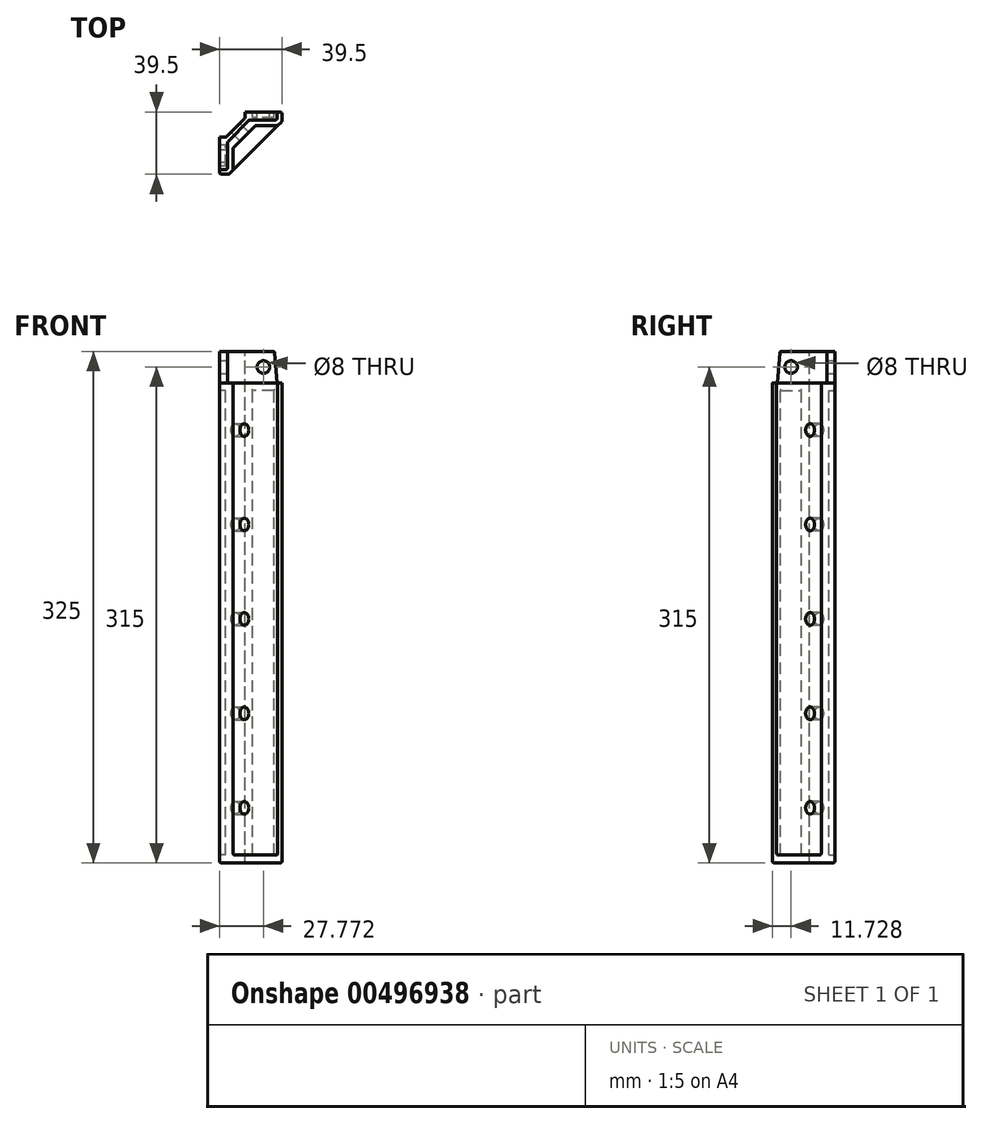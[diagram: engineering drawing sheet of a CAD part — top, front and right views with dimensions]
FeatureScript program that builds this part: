
annotation { "Feature Type Name" : "Feature", "Feature Type Description" : "" }
export const myFeature = defineFeature(function(context is Context, id is Id, definition is map)
    precondition{}
    {
        {
            var Q0;
            Q0=qCreatedBy(makeId("Top.planeOp"),FACE);
            var sketch = newSketch(context, id + "F0", { "sketchPlane" : qUnion([Q0])});
            skLineSegment(sketch, "E0", {"start": v(0, 30.13) * mm, "end": v(0, -27.95) * mm, "construction": true});
            skLineSegment(sketch, "E1", {"start": v(-25.65, 0) * mm, "end": v(27.57, 0) * mm, "construction": true});
            skLineSegment(sketch, "E2.bottom", {"start": v(-19.75, 19.75) * mm, "end": v(19.75, 19.75) * mm});
            skLineSegment(sketch, "E2.top", {"start": v(-19.75, -19.75) * mm, "end": v(-13.75, -19.75) * mm});
            skLineSegment(sketch, "E2.left", {"start": v(-19.75, 19.75) * mm, "end": v(-19.75, -19.75) * mm});
            skLineSegment(sketch, "E2.right", {"start": v(19.75, 19.75) * mm, "end": v(19.75, 13.75) * mm});
            skLineSegment(sketch, "E3", {"start": v(-13.75, -19.75) * mm, "end": v(19.75, 13.75) * mm});
            skSolve(sketch);
        }
        {
            var Q0;
            Q0=qSketchRegion(id+"F0",true);
            extrude(context, id + "F1", {"entities" : qUnion([Q0]), "oppositeDirection" : true, "depth" : 305 * mm, "symmetric" : true});
        }
        {
            var Q0;
            Q0=makeQuery(id+"F1.opExtrude","CAP_FACE",FACE,{"disambiguationData":[OSD([sQuery(id+"F0.wireOp",EDGE,"E2.bottom"),sQuery(id+"F0.wireOp",EDGE,"E2.top"),sQuery(id+"F0.wireOp",EDGE,"E2.left"),sQuery(id+"F0.wireOp",EDGE,"E2.right"),sQuery(id+"F0.wireOp",EDGE,"E3")])],"isStart":true});
            var sketch = newSketch(context, id + "F2", { "sketchPlane" : qUnion([Q0])});
            skLineSegment(sketch, "E4", {"start": v(3, -3) * mm, "end": v(-19.75, 19.75) * mm, "construction": true});
            skLineSegment(sketch, "E5", {"start": v(3, -3) * mm, "end": v(17.14, 11.14) * mm});
            skLineSegment(sketch, "E6", {"start": v(3, -3) * mm, "end": v(-11.14, -17.14) * mm});
            skLineSegment(sketch, "E7", {"start": v(-11.14, -3) * mm, "end": v(3, 11.14) * mm});
            skLineSegment(sketch, "E8", {"start": v(-11.14, -17.14) * mm, "end": v(-11.14, -3) * mm});
            skLineSegment(sketch, "E9", {"start": v(3, 11.14) * mm, "end": v(17.14, 11.14) * mm});
            skSolve(sketch);
        }
        {
            var Q0;
            Q0=qSketchRegion(id+"F2",true);
            extrude(context, id + "F3", {"entities" : qUnion([Q0]), "operationType" : NewBodyOperationType.REMOVE, "oppositeDirection" : true, "depth" : 300 * mm});
        }
        {
            var Q0;
            Q0=makeQuery(id+"F1.opExtrude","CAP_FACE",FACE,{"disambiguationData":[OSD([sQuery(id+"F0.wireOp",EDGE,"E2.bottom"),sQuery(id+"F0.wireOp",EDGE,"E2.top"),sQuery(id+"F0.wireOp",EDGE,"E2.left"),sQuery(id+"F0.wireOp",EDGE,"E2.right"),sQuery(id+"F0.wireOp",EDGE,"E3")])],"isStart":true});
            var sketch = newSketch(context, id + "F4", { "sketchPlane" : qUnion([Q0])});
            skPoint(sketch, "E10.orphan", {"position": v(-19.75, -19.75) * mm});
            skPoint(sketch, "E11.orphan", {"position": v(19.75, 19.75) * mm});
            skLineSegment(sketch, "E12", {"start": v(-19.75, 19.75) * mm, "end": v(-4.07, 4.07) * mm, "construction": true});
            skLineSegment(sketch, "E13", {"start": v(-15.75, 3.7) * mm, "end": v(-19.75, 3.7) * mm});
            skLineSegment(sketch, "E14", {"start": v(-3.7, 15.75) * mm, "end": v(-3.7, 19.75) * mm});
            skLineSegment(sketch, "E15", {"start": v(-3.7, 19.75) * mm, "end": v(-19.75, 19.75) * mm});
            skLineSegment(sketch, "E16", {"start": v(-19.75, 19.75) * mm, "end": v(-19.75, 3.7) * mm});
            skLineSegment(sketch, "E17", {"start": v(-3.7, 15.75) * mm, "end": v(-15.75, 3.7) * mm});
            skPoint(sketch, "E18.orphan", {"position": v(-14.68, 3.7) * mm});
            skPoint(sketch, "E19.orphan", {"position": v(-3.7, 13.6) * mm});
            skSolve(sketch);
        }
        {
            var Q0;
            Q0=qSketchRegion(id+"F4",true);
            extrude(context, id + "F5", {"entities" : qUnion([Q0]), "operationType" : NewBodyOperationType.REMOVE, "endBound" : BoundingType.THROUGH_ALL, "oppositeDirection" : true, "depth" : 25 * mm});
        }
        {
            var Q0;
            Q0=makeQuery(id+"F1.opExtrude","CAP_FACE",FACE,{"disambiguationData":[OSD([sQuery(id+"F0.wireOp",EDGE,"E2.bottom"),sQuery(id+"F0.wireOp",EDGE,"E2.top"),sQuery(id+"F0.wireOp",EDGE,"E2.left"),sQuery(id+"F0.wireOp",EDGE,"E2.right"),sQuery(id+"F0.wireOp",EDGE,"E3")])],"isStart":true});
            var sketch = newSketch(context, id + "F6", { "sketchPlane" : qUnion([Q0])});
            skLineSegment(sketch, "E20.0", {"start": v(1.3, 16.14) * mm, "end": v(14.75, 16.14) * mm});
            skLineSegment(sketch, "E20.1", {"start": v(14.75, 19.75) * mm, "end": v(14.75, 16.14) * mm});
            skLineSegment(sketch, "E21.0", {"start": v(1.3, 16.14) * mm, "end": v(1.3, 19.75) * mm});
            skLineSegment(sketch, "E22", {"start": v(14.75, 19.75) * mm, "end": v(1.3, 19.75) * mm});
            skLineSegment(sketch, "E23.0", {"start": v(-16.14, -14.75) * mm, "end": v(-16.14, -1.3) * mm});
            skLineSegment(sketch, "E23.1", {"start": v(-19.75, -14.75) * mm, "end": v(-16.14, -14.75) * mm});
            skLineSegment(sketch, "E24.0", {"start": v(-16.14, -1.3) * mm, "end": v(-19.75, -1.3) * mm});
            skPoint(sketch, "E25.orphan", {"position": v(-12.53, -1.3) * mm});
            skLineSegment(sketch, "E26", {"start": v(-19.75, -14.75) * mm, "end": v(-19.75, -1.3) * mm});
            skSolve(sketch);
        }
        {
            var Q0;
            Q0=qSketchRegion(id+"F6",true);
            extrude(context, id + "F7", {"entities" : qUnion([Q0]), "operationType" : NewBodyOperationType.REMOVE, "endBound" : BoundingType.THROUGH_ALL, "oppositeDirection" : true, "depth" : 25 * mm});
        }
        {
            var Q0;
            {var subQ1=sQuery(id+"F0.wireOp",EDGE,"E2.right");var subQ4=sQuery(id+"F0.wireOp",EDGE,"E2.bottom");Q0=makeQuery(id+"F7.boolean.opBoolean","SPLIT",FACE,{"disambiguationData":[TD([makeQuery(id+"F1.opExtrude","SWEPT_FACE",FACE,{"disambiguationData":[OSD([subQ1])]})])],"derivedFrom":makeQuery(id+"F1.opExtrude","SWEPT_FACE",FACE,{"disambiguationData":[OSD([subQ4])]})});}
            var sketch = newSketch(context, id + "F8", { "sketchPlane" : qUnion([Q0])});
            skLineSegment(sketch, "E27.bottom", {"start": v(-14.75, 152.5) * mm, "end": v(-1.3, 152.5) * mm});
            skLineSegment(sketch, "E27.top", {"start": v(-14.75, 147.5) * mm, "end": v(-1.3, 147.5) * mm});
            skLineSegment(sketch, "E27.left", {"start": v(-14.75, 152.5) * mm, "end": v(-14.75, 147.5) * mm});
            skLineSegment(sketch, "E27.right", {"start": v(-1.3, 152.5) * mm, "end": v(-1.3, 147.5) * mm});
            skLineSegment(sketch, "E28.bottom", {"start": v(-14.75, -152.5) * mm, "end": v(-1.3, -152.5) * mm});
            skLineSegment(sketch, "E28.top", {"start": v(-14.75, -147.5) * mm, "end": v(-1.3, -147.5) * mm});
            skLineSegment(sketch, "E28.left", {"start": v(-14.75, -152.5) * mm, "end": v(-14.75, -147.5) * mm});
            skLineSegment(sketch, "E28.right", {"start": v(-1.3, -152.5) * mm, "end": v(-1.3, -147.5) * mm});
            skSolve(sketch);
        }
        {
            var Q0;
            Q0=qSketchRegion(id+"F8",true);
            var Q1;
            Q1=makeQuery(id+"F7.boolean.opBoolean","COPY",FACE,{"derivedFrom":makeQuery(id+"F7.opExtrude","SWEPT_FACE",FACE,{"disambiguationData":[OSD([sQuery(id+"F6.wireOp",EDGE,"E20.0")])]})});
            extrude(context, id + "F9", {"entities" : qUnion([Q0]), "operationType" : NewBodyOperationType.ADD, "endBound" : BoundingType.UP_TO_SURFACE, "oppositeDirection" : true, "endBoundEntityFace" : qUnion([Q1]), "depth" : 25 * mm});
        }
        {
            var Q0;
            {var subQ2=sQuery(id+"F0.wireOp",EDGE,"E2.left");var subQ3=sQuery(id+"F0.wireOp",EDGE,"E2.top");Q0=makeQuery(id+"F7.boolean.opBoolean","SPLIT",FACE,{"disambiguationData":[TD([makeQuery(id+"F1.opExtrude","SWEPT_FACE",FACE,{"disambiguationData":[OSD([subQ3])]})])],"derivedFrom":makeQuery(id+"F1.opExtrude","SWEPT_FACE",FACE,{"disambiguationData":[OSD([subQ2])]})});}
            var sketch = newSketch(context, id + "F10", { "sketchPlane" : qUnion([Q0])});
            skLineSegment(sketch, "E29.bottom", {"start": v(14.75, 152.5) * mm, "end": v(1.3, 152.5) * mm});
            skLineSegment(sketch, "E29.top", {"start": v(14.75, 147.5) * mm, "end": v(1.3, 147.5) * mm});
            skLineSegment(sketch, "E29.left", {"start": v(14.75, 152.5) * mm, "end": v(14.75, 147.5) * mm});
            skLineSegment(sketch, "E29.right", {"start": v(1.3, 152.5) * mm, "end": v(1.3, 147.5) * mm});
            skLineSegment(sketch, "E30.bottom", {"start": v(14.75, -152.5) * mm, "end": v(1.3, -152.5) * mm});
            skLineSegment(sketch, "E30.top", {"start": v(14.75, -147.5) * mm, "end": v(1.3, -147.5) * mm});
            skLineSegment(sketch, "E30.left", {"start": v(14.75, -152.5) * mm, "end": v(14.75, -147.5) * mm});
            skLineSegment(sketch, "E30.right", {"start": v(1.3, -152.5) * mm, "end": v(1.3, -147.5) * mm});
            skSolve(sketch);
        }
        {
            var Q0;
            Q0=qSketchRegion(id+"F10",true);
            var Q1;
            Q1=makeQuery(id+"F7.boolean.opBoolean","COPY",FACE,{"derivedFrom":makeQuery(id+"F7.opExtrude","SWEPT_FACE",FACE,{"disambiguationData":[OSD([sQuery(id+"F6.wireOp",EDGE,"E23.0")])]})});
            extrude(context, id + "F11", {"entities" : qUnion([Q0]), "operationType" : NewBodyOperationType.ADD, "endBound" : BoundingType.UP_TO_SURFACE, "oppositeDirection" : true, "endBoundEntityFace" : qUnion([Q1]), "depth" : 25 * mm});
        }
        {
            var Q0;
            {var subQ2=sQuery(id+"F0.wireOp",EDGE,"E2.left");var subQ3=sQuery(id+"F0.wireOp",EDGE,"E2.top");var subQ7=makeQuery(id+"F1.opExtrude","SWEPT_FACE",FACE,{"disambiguationData":[OSD([subQ2])]});Q0=makeQuery(id+"F11.boolean.opBoolean","MERGE",FACE,{"derivedFrom":[makeQuery(id+"F7.boolean.opBoolean","SPLIT",FACE,{"disambiguationData":[TD([makeQuery(id+"F1.opExtrude","SWEPT_FACE",FACE,{"disambiguationData":[OSD([subQ3])]})])],"derivedFrom":subQ7}),makeQuery(id+"F7.boolean.opBoolean","SPLIT",FACE,{"disambiguationData":[TD([makeQuery(id+"F5.boolean.opBoolean","COPY",FACE,{"derivedFrom":makeQuery(id+"F5.opExtrude","SWEPT_FACE",FACE,{"disambiguationData":[OSD([sQuery(id+"F4.wireOp",EDGE,"E13")])]})})])],"derivedFrom":subQ7}),makeQuery(id+"F11.opExtrude","CAP_FACE",FACE,{"disambiguationData":[OSD([sQuery(id+"F10.wireOp",EDGE,"E29.bottom"),sQuery(id+"F10.wireOp",EDGE,"E29.top"),sQuery(id+"F10.wireOp",EDGE,"E29.left"),sQuery(id+"F10.wireOp",EDGE,"E29.right")])],"isStart":true}),makeQuery(id+"F11.opExtrude","CAP_FACE",FACE,{"disambiguationData":[OSD([sQuery(id+"F10.wireOp",EDGE,"E30.bottom"),sQuery(id+"F10.wireOp",EDGE,"E30.top"),sQuery(id+"F10.wireOp",EDGE,"E30.left"),sQuery(id+"F10.wireOp",EDGE,"E30.right")])],"isStart":true})]});}
            var sketch = newSketch(context, id + "F12", { "sketchPlane" : qUnion([Q0])});
            skLineSegment(sketch, "E31", {"start": v(8.02, 152.5) * mm, "end": v(8.02, 172.5) * mm, "construction": true});
            skLineSegment(sketch, "E32", {"start": v(0, 0) * mm, "end": v(35.4, 0) * mm, "construction": true});
            skPoint(sketch, "E32.endSnap0", {"position": v(19.75, 0) * mm});
            skLineSegment(sketch, "E33.MirrorCS", {"start": v(16.04, 0) * mm, "end": v(-19.35, 0) * mm, "construction": true});
            skLineSegment(sketch, "E34", {"start": v(16.75, 152.5) * mm, "end": v(-0.7, 152.5) * mm});
            skLineSegment(sketch, "E35", {"start": v(16.75, 152.5) * mm, "end": v(15.02, 172.5) * mm});
            skLineSegment(sketch, "E36", {"start": v(15.02, 172.5) * mm, "end": v(8.02, 172.5) * mm});
            skLineSegment(sketch, "E37", {"start": v(8.02, 172.5) * mm, "end": v(1.02, 172.5) * mm});
            skLineSegment(sketch, "E38", {"start": v(1.02, 172.5) * mm, "end": v(-0.7, 152.5) * mm});
            skLineSegment(sketch, "E39.MirrorCS", {"start": v(-0.7, 152.5) * mm, "end": v(1.02, 172.5) * mm});
            skSolve(sketch);
        }
        {
            var Q0;
            Q0=qSketchRegion(id+"F12",true);
            extrude(context, id + "F13", {"entities" : qUnion([Q0]), "operationType" : NewBodyOperationType.ADD, "oppositeDirection" : true, "depth" : 5 * mm});
        }
        {
            var Q0;
            {var subQ1=sQuery(id+"F0.wireOp",EDGE,"E2.right");var subQ4=sQuery(id+"F0.wireOp",EDGE,"E2.bottom");var subQ7=makeQuery(id+"F1.opExtrude","SWEPT_FACE",FACE,{"disambiguationData":[OSD([subQ4])]});Q0=makeQuery(id+"F9.boolean.opBoolean","MERGE",FACE,{"derivedFrom":[makeQuery(id+"F7.boolean.opBoolean","SPLIT",FACE,{"disambiguationData":[TD([makeQuery(id+"F1.opExtrude","SWEPT_FACE",FACE,{"disambiguationData":[OSD([subQ1])]})])],"derivedFrom":subQ7}),makeQuery(id+"F7.boolean.opBoolean","SPLIT",FACE,{"disambiguationData":[TD([makeQuery(id+"F5.boolean.opBoolean","COPY",FACE,{"derivedFrom":makeQuery(id+"F5.opExtrude","SWEPT_FACE",FACE,{"disambiguationData":[OSD([sQuery(id+"F4.wireOp",EDGE,"E14")])]})})])],"derivedFrom":subQ7}),makeQuery(id+"F9.opExtrude","CAP_FACE",FACE,{"disambiguationData":[OSD([sQuery(id+"F8.wireOp",EDGE,"E27.bottom"),sQuery(id+"F8.wireOp",EDGE,"E27.top"),sQuery(id+"F8.wireOp",EDGE,"E27.left"),sQuery(id+"F8.wireOp",EDGE,"E27.right")])],"isStart":true}),makeQuery(id+"F9.opExtrude","CAP_FACE",FACE,{"disambiguationData":[OSD([sQuery(id+"F8.wireOp",EDGE,"E28.bottom"),sQuery(id+"F8.wireOp",EDGE,"E28.top"),sQuery(id+"F8.wireOp",EDGE,"E28.left"),sQuery(id+"F8.wireOp",EDGE,"E28.right")])],"isStart":true})]});}
            var sketch = newSketch(context, id + "F14", { "sketchPlane" : qUnion([Q0])});
            skLineSegment(sketch, "E40", {"start": v(-8.02, 152.5) * mm, "end": v(-8.02, 172.66) * mm, "construction": true});
            skPoint(sketch, "E40.endSnap0", {"position": v(-8.02, 152.5) * mm});
            skLineSegment(sketch, "E41", {"start": v(-15.02, 172.5) * mm, "end": v(-1.02, 172.5) * mm});
            skLineSegment(sketch, "E42", {"start": v(0, 0) * mm, "end": v(-60.6, 0) * mm, "construction": true});
            skPoint(sketch, "E42.endSnap0", {"position": v(-14.75, 0) * mm});
            skLineSegment(sketch, "E43", {"start": v(-15.02, 172.5) * mm, "end": v(-16.75, 152.5) * mm});
            skLineSegment(sketch, "E44", {"start": v(-1.02, 172.5) * mm, "end": v(0.7, 152.5) * mm});
            skLineSegment(sketch, "E45", {"start": v(0.7, 152.5) * mm, "end": v(-16.75, 152.5) * mm});
            skSolve(sketch);
        }
        {
            var Q0;
            Q0=qSketchRegion(id+"F14",true);
            extrude(context, id + "F15", {"entities" : qUnion([Q0]), "operationType" : NewBodyOperationType.ADD, "oppositeDirection" : true, "depth" : 5 * mm});
        }
        {
            var Q0;
            {var subQ1=sQuery(id+"F0.wireOp",EDGE,"E2.right");var subQ4=sQuery(id+"F0.wireOp",EDGE,"E2.bottom");var subQ7=makeQuery(id+"F1.opExtrude","SWEPT_FACE",FACE,{"disambiguationData":[OSD([subQ4])]});Q0=makeQuery(id+"F15.boolean.opBoolean","MERGE",FACE,{"derivedFrom":[makeQuery(id+"F9.boolean.opBoolean","MERGE",FACE,{"derivedFrom":[makeQuery(id+"F7.boolean.opBoolean","SPLIT",FACE,{"disambiguationData":[TD([makeQuery(id+"F1.opExtrude","SWEPT_FACE",FACE,{"disambiguationData":[OSD([subQ1])]})])],"derivedFrom":subQ7}),makeQuery(id+"F7.boolean.opBoolean","SPLIT",FACE,{"disambiguationData":[TD([makeQuery(id+"F5.boolean.opBoolean","COPY",FACE,{"derivedFrom":makeQuery(id+"F5.opExtrude","SWEPT_FACE",FACE,{"disambiguationData":[OSD([sQuery(id+"F4.wireOp",EDGE,"E14")])]})})])],"derivedFrom":subQ7}),makeQuery(id+"F9.opExtrude","CAP_FACE",FACE,{"disambiguationData":[OSD([sQuery(id+"F8.wireOp",EDGE,"E27.bottom"),sQuery(id+"F8.wireOp",EDGE,"E27.top"),sQuery(id+"F8.wireOp",EDGE,"E27.left"),sQuery(id+"F8.wireOp",EDGE,"E27.right")])],"isStart":true}),makeQuery(id+"F9.opExtrude","CAP_FACE",FACE,{"disambiguationData":[OSD([sQuery(id+"F8.wireOp",EDGE,"E28.bottom"),sQuery(id+"F8.wireOp",EDGE,"E28.top"),sQuery(id+"F8.wireOp",EDGE,"E28.left"),sQuery(id+"F8.wireOp",EDGE,"E28.right")])],"isStart":true})]}),makeQuery(id+"F15.opExtrude","CAP_FACE",FACE,{"disambiguationData":[OSD([sQuery(id+"F14.wireOp",EDGE,"AjdLOBUI-PND2-HRux-vW9i-I60BuJFxOAxo"),sQuery(id+"F14.wireOp",EDGE,"m2E0O1S7-ugW4-w8lP-xUBK-8UGrL3XVD3p1"),sQuery(id+"F14.wireOp",EDGE,"E41"),sQuery(id+"F14.wireOp",EDGE,"z751VbyZ-Eswl-sp4i-D6d8-2ebrKqnJ25gN")])],"isStart":true}),makeQuery(id+"F15.opExtrude","CAP_FACE",FACE,{"disambiguationData":[OSD([sQuery(id+"F14.wireOp",EDGE,"9fced805-f766-4b14-a849-f1590210c0c81.MirrorCS"),sQuery(id+"F14.wireOp",EDGE,"9fced805-f766-4b14-a849-f1590210c0c82.MirrorCS"),sQuery(id+"F14.wireOp",EDGE,"9fced805-f766-4b14-a849-f1590210c0c83.MirrorCS"),sQuery(id+"F14.wireOp",EDGE,"9fced805-f766-4b14-a849-f1590210c0c84.MirrorCS")])],"isStart":true})]});}
            var sketch = newSketch(context, id + "F16", { "sketchPlane" : qUnion([Q0])});
            skLineSegment(sketch, "E46", {"start": v(-8.02, 172.5) * mm, "end": v(-8.02, -66.14) * mm, "construction": true});
            skCircle(sketch, "E47", {"center": v(-8.02, 162.5) * mm, "radius": 4 * mm});
            skSolve(sketch);
        }
        {
            var Q0;
            Q0=qSketchRegion(id+"F16",true);
            extrude(context, id + "F17", {"entities" : qUnion([Q0]), "operationType" : NewBodyOperationType.REMOVE, "endBound" : BoundingType.THROUGH_ALL, "oppositeDirection" : true, "depth" : 25 * mm});
        }
        {
            var Q0;
            Q0=makeQuery(id+"F3.boolean.opBoolean","COPY",FACE,{"derivedFrom":makeQuery(id+"F3.opExtrude","SWEPT_FACE",FACE,{"disambiguationData":[OSD([sQuery(id+"F2.wireOp",EDGE,"E7")])]})});
            var sketch = newSketch(context, id + "F18", { "sketchPlane" : qUnion([Q0])});
            skLineSegment(sketch, "E48", {"start": v(0, 152.5) * mm, "end": v(0, -147.5) * mm, "construction": true});
            skLineSegment(sketch, "E49", {"start": v(0, 2.5) * mm, "end": v(10, 2.5) * mm, "construction": true});
            skCircle(sketch, "E50", {"center": v(0, 122.5) * mm, "radius": 4 * mm});
            skCircle(sketch, "E51", {"center": v(0, 62.5) * mm, "radius": 4 * mm});
            skCircle(sketch, "E52.MirrorC", {"center": v(0, -117.5) * mm, "radius": 4 * mm});
            skCircle(sketch, "E53.MirrorC", {"center": v(0, -57.5) * mm, "radius": 4 * mm});
            skCircle(sketch, "E54", {"center": v(0, 2.5) * mm, "radius": 4 * mm});
            skSolve(sketch);
        }
        {
            var Q0;
            Q0=qSketchRegion(id+"F18",true);
            extrude(context, id + "F19", {"entities" : qUnion([Q0]), "operationType" : NewBodyOperationType.REMOVE, "endBound" : BoundingType.THROUGH_ALL, "oppositeDirection" : true, "depth" : 25 * mm});
        }
        {
            var Q0;
            Q0=makeQuery(id+"F13.opExtrude","CAP_FACE",FACE,{"disambiguationData":[OSD([sQuery(id+"F12.wireOp",EDGE,"E34"),sQuery(id+"F12.wireOp",EDGE,"E35"),sQuery(id+"F12.wireOp",EDGE,"E36"),sQuery(id+"F12.wireOp",EDGE,"E37"),sQuery(id+"F12.wireOp",EDGE,"E39.MirrorCS")])],"isStart":false});
            var sketch = newSketch(context, id + "F20", { "sketchPlane" : qUnion([Q0])});
            skLineSegment(sketch, "E55", {"start": v(-8.02, 172.5) * mm, "end": v(-8.02, -22.5) * mm, "construction": true});
            skPoint(sketch, "E55.endSnap0", {"position": v(-8.02, 172.5) * mm});
            skCircle(sketch, "E56", {"center": v(-8.02, 162.5) * mm, "radius": 4 * mm});
            skSolve(sketch);
        }
        {
            var Q0;
            Q0=qSketchRegion(id+"F20",true);
            extrude(context, id + "F21", {"entities" : qUnion([Q0]), "operationType" : NewBodyOperationType.REMOVE, "endBound" : BoundingType.THROUGH_ALL, "oppositeDirection" : true, "depth" : 25 * mm});
        }
        {
            var Q0;
            Q0=makeQuery(id+"F11.boolean.opBoolean","MERGE",FACE,{"derivedFrom":[makeQuery(id+"F9.boolean.opBoolean","MERGE",FACE,{"derivedFrom":[makeQuery(id+"F1.opExtrude","CAP_FACE",FACE,{"disambiguationData":[OSD([sQuery(id+"F0.wireOp",EDGE,"E2.bottom"),sQuery(id+"F0.wireOp",EDGE,"E2.top"),sQuery(id+"F0.wireOp",EDGE,"E2.left"),sQuery(id+"F0.wireOp",EDGE,"E2.right"),sQuery(id+"F0.wireOp",EDGE,"E3")])],"isStart":true}),makeQuery(id+"F9.opExtrude","SWEPT_FACE",FACE,{"disambiguationData":[OSD([sQuery(id+"F8.wireOp",EDGE,"E27.bottom")])]})]}),makeQuery(id+"F11.opExtrude","SWEPT_FACE",FACE,{"disambiguationData":[OSD([sQuery(id+"F10.wireOp",EDGE,"E29.bottom")])]})]});
            var sketch = newSketch(context, id + "F22", { "sketchPlane" : qUnion([Q0])});
            skLineSegment(sketch, "E57.0", {"start": v(-0.7, 14.75) * mm, "end": v(-0.7, 19.75) * mm});
            skPoint(sketch, "E58.0", {"position": v(-2.2, 19.75) * mm});
            skLineSegment(sketch, "E59.0", {"start": v(-3.7, 19.75) * mm, "end": v(-0.7, 19.75) * mm});
            skLineSegment(sketch, "E60.0", {"start": v(-3.7, 15.75) * mm, "end": v(-3.7, 19.75) * mm});
            skLineSegment(sketch, "E61.0", {"start": v(-3.7, 15.75) * mm, "end": v(-15.75, 3.7) * mm});
            skLineSegment(sketch, "E62.0", {"start": v(-15.75, 3.7) * mm, "end": v(-19.75, 3.7) * mm});
            skLineSegment(sketch, "E63.0", {"start": v(-19.75, 3.7) * mm, "end": v(-19.75, 0.7) * mm});
            skLineSegment(sketch, "E64.0", {"start": v(-14.75, 0.7) * mm, "end": v(-19.75, 0.7) * mm});
            skPoint(sketch, "E65.orphan", {"position": v(1.02, 14.75) * mm});
            skLineSegment(sketch, "E66", {"start": v(-14.75, 0.7) * mm, "end": v(-0.7, 14.75) * mm});
            skSolve(sketch);
        }
        {
            var Q0;
            Q0=qSketchRegion(id+"F22",true);
            extrude(context, id + "F23", {"entities" : qUnion([Q0]), "operationType" : NewBodyOperationType.ADD, "depth" : 20 * mm});
        }
        {
            var Q0;
            Q0=makeQuery(id+"F13.opExtrude","SWEPT_FACE",FACE,{"disambiguationData":[OSD([sQuery(id+"F12.wireOp",EDGE,"E36"),sQuery(id+"F12.wireOp",EDGE,"E37")])]});
            var sketch = newSketch(context, id + "F24", { "sketchPlane" : qUnion([Q0])});
            skLineSegment(sketch, "E67.0.0", {"start": v(-19.75, 0.7) * mm, "end": v(-19.75, -1.02) * mm});
            skLineSegment(sketch, "E67.0.1", {"start": v(-19.75, -1.02) * mm, "end": v(-14.75, -1.02) * mm});
            skLineSegment(sketch, "E67.0.2", {"start": v(-14.75, -1.02) * mm, "end": v(-14.75, 0.7) * mm});
            skLineSegment(sketch, "E67.0.3", {"start": v(-14.75, 0.7) * mm, "end": v(-19.75, 0.7) * mm});
            skLineSegment(sketch, "E68.0.0", {"start": v(1.02, 19.75) * mm, "end": v(-0.7, 19.75) * mm});
            skLineSegment(sketch, "E68.0.1", {"start": v(-0.7, 19.75) * mm, "end": v(-0.7, 14.75) * mm});
            skLineSegment(sketch, "E68.0.2", {"start": v(-0.7, 14.75) * mm, "end": v(1.02, 14.75) * mm});
            skLineSegment(sketch, "E68.0.3", {"start": v(1.02, 14.75) * mm, "end": v(1.02, 19.75) * mm});
            skSolve(sketch);
        }
        {
            var Q0;
            Q0=qSketchRegion(id+"F24",true);
            extrude(context, id + "F25", {"entities" : qUnion([Q0]), "operationType" : NewBodyOperationType.ADD, "oppositeDirection" : true, "depth" : 25 * mm});
        }
        {
            var Q0;
            Q0=makeQuery(id+"F13.opExtrude","SWEPT_EDGE",EDGE,{"disambiguationData":[OSD([sQuery(id+"F12.wireOp",EDGE,"E35"),sQuery(id+"F12.wireOp",EDGE,"E36")])]});
            var Q1;
            Q1=makeQuery(id+"F13.opExtrude","SWEPT_EDGE",EDGE,{"disambiguationData":[OSD([sQuery(id+"F12.wireOp",EDGE,"E37"),sQuery(id+"F12.wireOp",EDGE,"E39.MirrorCS")])]});
            var Q2;
            Q2=makeQuery(id+"F15.opExtrude","SWEPT_EDGE",EDGE,{"disambiguationData":[OSD([sQuery(id+"F14.wireOp",EDGE,"E41"),sQuery(id+"F14.wireOp",EDGE,"E43")])]});
            var Q3;
            Q3=makeQuery(id+"F15.opExtrude","SWEPT_EDGE",EDGE,{"disambiguationData":[OSD([sQuery(id+"F14.wireOp",EDGE,"E41"),sQuery(id+"F14.wireOp",EDGE,"E44")])]});
            var Q4;
            Q4=makeQuery(id+"F15.opExtrude","SWEPT_EDGE",EDGE,{"disambiguationData":[OSD([sQuery(id+"F14.wireOp",EDGE,"14d68a54-c34f-48c8-ae77-41faf57796821.MirrorCS"),sQuery(id+"F14.wireOp",EDGE,"14d68a54-c34f-48c8-ae77-41faf57796823.MirrorCS")])]});
            var Q5;
            Q5=makeQuery(id+"F15.opExtrude","SWEPT_EDGE",EDGE,{"disambiguationData":[OSD([sQuery(id+"F14.wireOp",EDGE,"14d68a54-c34f-48c8-ae77-41faf57796820.MirrorCS"),sQuery(id+"F14.wireOp",EDGE,"14d68a54-c34f-48c8-ae77-41faf57796823.MirrorCS")])]});
            var Q6;
            Q6=makeQuery(id+"F13.opExtrude","SWEPT_EDGE",EDGE,{"disambiguationData":[OSD([sQuery(id+"F12.wireOp",EDGE,"0e25475b-3a4a-4502-b2ef-1a4ccfbb12351.MirrorCS"),sQuery(id+"F12.wireOp",EDGE,"0e25475b-3a4a-4502-b2ef-1a4ccfbb12353.MirrorCS")])]});
            var Q7;
            Q7=makeQuery(id+"F13.opExtrude","SWEPT_EDGE",EDGE,{"disambiguationData":[OSD([sQuery(id+"F12.wireOp",EDGE,"0e25475b-3a4a-4502-b2ef-1a4ccfbb12352.MirrorCS"),sQuery(id+"F12.wireOp",EDGE,"0e25475b-3a4a-4502-b2ef-1a4ccfbb12353.MirrorCS")])]});
            var Q8;
            Q8=makeQuery(id+"F1.opExtrude","SWEPT_EDGE",EDGE,{"disambiguationData":[OSD([sQuery(id+"F0.wireOp",EDGE,"E2.top"),sQuery(id+"F0.wireOp",EDGE,"E3")])]});
            var Q9;
            Q9=makeQuery(id+"F1.opExtrude","SWEPT_EDGE",EDGE,{"disambiguationData":[OSD([sQuery(id+"F0.wireOp",EDGE,"E2.right"),sQuery(id+"F0.wireOp",EDGE,"E3")])]});
            var Q10;
            Q10=makeQuery(id+"F3.boolean.opBoolean","COPY",EDGE,{"derivedFrom":makeQuery(id+"F3.opExtrude","SWEPT_EDGE",EDGE,{"disambiguationData":[OSD([sQuery(id+"F2.wireOp",EDGE,"E7"),sQuery(id+"F2.wireOp",EDGE,"E8")])]})});
            var Q11;
            Q11=makeQuery(id+"F3.boolean.opBoolean","COPY",EDGE,{"derivedFrom":makeQuery(id+"F3.opExtrude","SWEPT_EDGE",EDGE,{"disambiguationData":[OSD([sQuery(id+"F2.wireOp",EDGE,"E7"),sQuery(id+"F2.wireOp",EDGE,"E9")])]})});
            var Q12;
            Q12=makeQuery(id+"F5.boolean.opBoolean","COPY",EDGE,{"derivedFrom":makeQuery(id+"F5.opExtrude","SWEPT_EDGE",EDGE,{"disambiguationData":[OSD([sQuery(id+"F4.wireOp",EDGE,"E13"),sQuery(id+"F4.wireOp",EDGE,"E17")])]})});
            var Q13;
            Q13=makeQuery(id+"F5.boolean.opBoolean","COPY",EDGE,{"derivedFrom":makeQuery(id+"F5.opExtrude","SWEPT_EDGE",EDGE,{"disambiguationData":[OSD([sQuery(id+"F4.wireOp",EDGE,"E14"),sQuery(id+"F4.wireOp",EDGE,"E17")])]})});
            var Q14;
            Q14=makeQuery(id+"F5.boolean.opBoolean","COPY",EDGE,{"derivedFrom":makeQuery(id+"F5.opExtrude","SWEPT_EDGE",EDGE,{"disambiguationData":[OSD([sQuery(id+"F0.wireOp",EDGE,"E2.bottom"),sQuery(id+"F4.wireOp",EDGE,"E14"),sQuery(id+"F4.wireOp",EDGE,"E15")])]})});
            var Q15;
            Q15=makeQuery(id+"F5.boolean.opBoolean","COPY",EDGE,{"derivedFrom":makeQuery(id+"F5.opExtrude","SWEPT_EDGE",EDGE,{"disambiguationData":[OSD([sQuery(id+"F0.wireOp",EDGE,"E2.left"),sQuery(id+"F4.wireOp",EDGE,"E13"),sQuery(id+"F4.wireOp",EDGE,"E16")])]})});
            var Q16;
            Q16=makeQuery(id+"F11.opExtrude","SWEPT_EDGE",EDGE,{"disambiguationData":[OSD([sQuery(id+"F0.wireOp",EDGE,"E2.left"),sQuery(id+"F6.wireOp",EDGE,"E23.1"),sQuery(id+"F6.wireOp",EDGE,"E26"),sQuery(id+"F10.wireOp",EDGE,"E29.top"),sQuery(id+"F10.wireOp",EDGE,"E29.left")])]});
            var Q17;
            Q17=makeQuery(id+"F11.opExtrude","SWEPT_EDGE",EDGE,{"disambiguationData":[OSD([sQuery(id+"F10.wireOp",EDGE,"E29.top"),sQuery(id+"F10.wireOp",EDGE,"E29.right")])]});
            var Q18;
            Q18=makeQuery(id+"F11.opExtrude","SWEPT_EDGE",EDGE,{"disambiguationData":[OSD([sQuery(id+"F10.wireOp",EDGE,"E30.top"),sQuery(id+"F10.wireOp",EDGE,"E30.right")])]});
            var Q19;
            Q19=makeQuery(id+"F11.opExtrude","SWEPT_EDGE",EDGE,{"disambiguationData":[OSD([sQuery(id+"F0.wireOp",EDGE,"E2.left"),sQuery(id+"F6.wireOp",EDGE,"E23.1"),sQuery(id+"F6.wireOp",EDGE,"E26"),sQuery(id+"F10.wireOp",EDGE,"E30.top"),sQuery(id+"F10.wireOp",EDGE,"E30.left")])]});
            var Q20;
            Q20=makeQuery(id+"F9.opExtrude","SWEPT_EDGE",EDGE,{"disambiguationData":[OSD([sQuery(id+"F0.wireOp",EDGE,"E2.bottom"),sQuery(id+"F6.wireOp",EDGE,"E20.1"),sQuery(id+"F6.wireOp",EDGE,"E22"),sQuery(id+"F8.wireOp",EDGE,"E28.top"),sQuery(id+"F8.wireOp",EDGE,"E28.left")])]});
            var Q21;
            Q21=makeQuery(id+"F9.opExtrude","SWEPT_EDGE",EDGE,{"disambiguationData":[OSD([sQuery(id+"F8.wireOp",EDGE,"E28.top"),sQuery(id+"F8.wireOp",EDGE,"E28.right")])]});
            var Q22;
            Q22=makeQuery(id+"F9.opExtrude","SWEPT_EDGE",EDGE,{"disambiguationData":[OSD([sQuery(id+"F0.wireOp",EDGE,"E2.bottom"),sQuery(id+"F6.wireOp",EDGE,"E20.1"),sQuery(id+"F6.wireOp",EDGE,"E22"),sQuery(id+"F8.wireOp",EDGE,"E27.top"),sQuery(id+"F8.wireOp",EDGE,"E27.left")])]});
            var Q23;
            Q23=makeQuery(id+"F9.opExtrude","SWEPT_EDGE",EDGE,{"disambiguationData":[OSD([sQuery(id+"F8.wireOp",EDGE,"E27.top"),sQuery(id+"F8.wireOp",EDGE,"E27.right")])]});
            var Q24;
            Q24=makeQuery(id+"FQgWeVVyTOw4oP8_1.1.F13.opExtrude","SWEPT_EDGE",EDGE,{"disambiguationData":[OSD([sQuery(id+"F12.wireOp",EDGE,"E35"),sQuery(id+"F12.wireOp",EDGE,"E36")])]});
            var Q25;
            Q25=makeQuery(id+"F0G2RlgfnTVtGBU_1.1.F15.opExtrude","SWEPT_EDGE",EDGE,{"disambiguationData":[OSD([sQuery(id+"F14.wireOp",EDGE,"E41"),sQuery(id+"F14.wireOp",EDGE,"E43")])]});
            var Q26;
            Q26=makeQuery(id+"FlFclubRB8u2xVJ_1.1.F23.opExtrude","SWEPT_EDGE",EDGE,{"disambiguationData":[OSD([sQuery(id+"F22.wireOp",EDGE,"13f4e866-1eac-4fd2-8cb8-b31731ec45be.0"),sQuery(id+"F22.wireOp",EDGE,"IEdAcdNN-kTPl-dZrz-dtDZ-8rgaU4BHqawl")])]});
            var Q27;
            Q27=makeQuery(id+"FlFclubRB8u2xVJ_1.1.F23.opExtrude","SWEPT_EDGE",EDGE,{"disambiguationData":[OSD([sQuery(id+"F22.wireOp",EDGE,"13f4e866-1eac-4fd2-8cb8-b31731ec45be.0"),sQuery(id+"F22.wireOp",EDGE,"EtFefJ2s-15CD-pvIh-Pjx4-gmoe8S5X5IGa")])]});
            var Q28;
            Q28=makeQuery(id+"F23.opExtrude","SWEPT_EDGE",EDGE,{"disambiguationData":[OSD([sQuery(id+"F22.wireOp",EDGE,"13f4e866-1eac-4fd2-8cb8-b31731ec45be.0"),sQuery(id+"F22.wireOp",EDGE,"EtFefJ2s-15CD-pvIh-Pjx4-gmoe8S5X5IGa")])]});
            var Q29;
            Q29=makeQuery(id+"F23.opExtrude","SWEPT_EDGE",EDGE,{"disambiguationData":[OSD([sQuery(id+"F22.wireOp",EDGE,"13f4e866-1eac-4fd2-8cb8-b31731ec45be.0"),sQuery(id+"F22.wireOp",EDGE,"IEdAcdNN-kTPl-dZrz-dtDZ-8rgaU4BHqawl")])]});
            fillet(context, id + "F26", {"entities" : qUnion([Q0, Q1, Q2, Q3, Q4, Q5, Q6, Q7, Q8, Q9, Q10, Q11, Q12, Q13, Q14, Q15, Q16, Q17, Q18, Q19, Q20, Q21, Q22, Q23, Q24, Q25, Q26, Q27, Q28, Q29]), "radius" : 1 * mm, "tangentPropagation" : true, "allowEdgeOverflow" : false});
        }
        {
            var Q0;
            Q0=makeQuery(id+"F25.opExtrude","SWEPT_EDGE",EDGE,{"disambiguationData":[OSD([sQuery(id+"F24.wireOp",EDGE,"E67.0.2"),sQuery(id+"F24.wireOp",EDGE,"E67.0.3")])]});
            var Q1;
            Q1=makeQuery(id+"F25.opExtrude","SWEPT_EDGE",EDGE,{"disambiguationData":[OSD([sQuery(id+"F24.wireOp",EDGE,"E68.0.1"),sQuery(id+"F24.wireOp",EDGE,"E68.0.2")])]});
            var Q2;
            Q2=makeQuery(id+"FP1PUGvhXahgOBu_1.1.F25.opExtrude","SWEPT_EDGE",EDGE,{"disambiguationData":[OSD([sQuery(id+"F24.wireOp",EDGE,"E67.0.2"),sQuery(id+"F24.wireOp",EDGE,"E67.0.3")])]});
            var Q3;
            Q3=makeQuery(id+"FP1PUGvhXahgOBu_1.1.F25.opExtrude","SWEPT_EDGE",EDGE,{"disambiguationData":[OSD([sQuery(id+"F24.wireOp",EDGE,"E68.0.1"),sQuery(id+"F24.wireOp",EDGE,"E68.0.2")])]});
            fillet(context, id + "F27", {"entities" : qUnion([Q0, Q1, Q2, Q3]), "radius" : 1 * mm, "tangentPropagation" : true, "allowEdgeOverflow" : false});
        }
        {
            var Q0;
            Q0=makeQuery(id+"F3.boolean.opBoolean","COPY",EDGE,{"derivedFrom":makeQuery(id+"F3.opExtrude","CAP_EDGE",EDGE,{"disambiguationData":[OSD([sQuery(id+"F2.wireOp",EDGE,"E8")])],"isStart":false})});
            var Q1;
            Q1=makeQuery(id+"F9.opExtrude","TWEAK_EDGE",EDGE,{"derivedFrom":[makeQuery(id+"F7.boolean.opBoolean","COPY",FACE,{"derivedFrom":makeQuery(id+"F7.opExtrude","SWEPT_FACE",FACE,{"disambiguationData":[OSD([sQuery(id+"F6.wireOp",EDGE,"E20.0")])]})}),makeQuery(id+"F8.imprint","IMPRINT",EDGE,{"derivedFrom":sQuery(id+"F8.wireOp",EDGE,"E27.top")})]});
            var Q2;
            Q2=makeQuery(id+"F9.opExtrude","CAP_EDGE",EDGE,{"disambiguationData":[OSD([sQuery(id+"F8.wireOp",EDGE,"E27.top")])],"isStart":true});
            var Q3;
            Q3=makeQuery(id+"F11.opExtrude","TWEAK_EDGE",EDGE,{"derivedFrom":[makeQuery(id+"F7.boolean.opBoolean","COPY",FACE,{"derivedFrom":makeQuery(id+"F7.opExtrude","SWEPT_FACE",FACE,{"disambiguationData":[OSD([sQuery(id+"F6.wireOp",EDGE,"E23.0")])]})}),makeQuery(id+"F10.imprint","IMPRINT",EDGE,{"derivedFrom":sQuery(id+"F10.wireOp",EDGE,"E29.top")})]});
            var Q4;
            Q4=makeQuery(id+"F11.opExtrude","CAP_EDGE",EDGE,{"disambiguationData":[OSD([sQuery(id+"F10.wireOp",EDGE,"E29.top")])],"isStart":true});
            var Q5;
            Q5=makeQuery(id+"FQgWeVVyTOw4oP8_1.1.F13.opExtrude","CAP_EDGE",EDGE,{"disambiguationData":[OSD([sQuery(id+"F12.wireOp",EDGE,"E35")])],"isStart":false});
            var Q6;
            Q6=makeQuery(id+"F13.opExtrude","CAP_EDGE",EDGE,{"disambiguationData":[OSD([sQuery(id+"F12.wireOp",EDGE,"E35")])],"isStart":false});
            fillet(context, id + "F28", {"entities" : qUnion([Q0, Q1, Q2, Q3, Q4, Q5, Q6]), "radius" : 1 * mm, "tangentPropagation" : true, "allowEdgeOverflow" : false});
        }
        {
            var Q0;
            Q0=makeQuery(id+"F3.boolean.opBoolean","COPY",EDGE,{"derivedFrom":makeQuery(id+"F3.opExtrude","SWEPT_EDGE",EDGE,{"disambiguationData":[OSD([sQuery(id+"F0.wireOp",EDGE,"E3"),sQuery(id+"F2.wireOp",EDGE,"E6"),sQuery(id+"F2.wireOp",EDGE,"E8")])]})});
            var Q1;
            Q1=makeQuery(id+"F13.opExtrude","SWEPT_EDGE",EDGE,{"disambiguationData":[OSD([sQuery(id+"F0.wireOp",EDGE,"E2.left"),sQuery(id+"F10.wireOp",EDGE,"E29.bottom"),sQuery(id+"F12.wireOp",EDGE,"E34"),sQuery(id+"F12.wireOp",EDGE,"E35")])]});
            var Q2;
            Q2=makeQuery(id+"F15.opExtrude","SWEPT_EDGE",EDGE,{"disambiguationData":[OSD([sQuery(id+"F0.wireOp",EDGE,"E2.bottom"),sQuery(id+"F8.wireOp",EDGE,"E27.bottom"),sQuery(id+"F14.wireOp",EDGE,"E43"),sQuery(id+"F14.wireOp",EDGE,"E45")])]});
            var Q3;
            Q3=makeQuery(id+"F13.opExtrude","SWEPT_EDGE",EDGE,{"disambiguationData":[OSD([sQuery(id+"F0.wireOp",EDGE,"E2.left"),sQuery(id+"F10.wireOp",EDGE,"E30.bottom"),sQuery(id+"F12.wireOp",EDGE,"0e25475b-3a4a-4502-b2ef-1a4ccfbb12352.MirrorCS"),sQuery(id+"F12.wireOp",EDGE,"0e25475b-3a4a-4502-b2ef-1a4ccfbb12354.MirrorCS")])]});
            var Q4;
            Q4=makeQuery(id+"F15.opExtrude","CAP_EDGE",EDGE,{"disambiguationData":[OSD([sQuery(id+"F14.wireOp",EDGE,"14d68a54-c34f-48c8-ae77-41faf57796822.MirrorCS")])],"isStart":false});
            var Q5;
            Q5=makeQuery(id+"F1.opExtrude","SWEPT_EDGE",EDGE,{"disambiguationData":[OSD([sQuery(id+"F0.wireOp",EDGE,"E2.bottom"),sQuery(id+"F0.wireOp",EDGE,"E2.right")])]});
            var Q6;
            Q6=makeQuery(id+"F1.opExtrude","SWEPT_EDGE",EDGE,{"disambiguationData":[OSD([sQuery(id+"F0.wireOp",EDGE,"E2.top"),sQuery(id+"F0.wireOp",EDGE,"E2.left")])]});
            var Q7;
            Q7=makeQuery(id+"F0G2RlgfnTVtGBU_1.1.F15.opExtrude","SWEPT_EDGE",EDGE,{"disambiguationData":[OSD([sQuery(id+"F0.wireOp",EDGE,"E2.bottom"),sQuery(id+"F8.wireOp",EDGE,"E27.bottom"),sQuery(id+"F14.wireOp",EDGE,"E43"),sQuery(id+"F14.wireOp",EDGE,"E45")])]});
            fillet(context, id + "F29", {"entities" : qUnion([Q0, Q1, Q2, Q3, Q4, Q5, Q6, Q7]), "radius" : 1 * mm, "tangentPropagation" : true, "allowEdgeOverflow" : false});
        }
        {
            var Q0;
            Q0=makeQuery(id+"F1.opExtrude","CAP_EDGE",EDGE,{"disambiguationData":[OSD([sQuery(id+"F0.wireOp",EDGE,"E2.top")])],"isStart":false});
            var Q1;
            Q1=makeQuery(id+"F3.boolean.opBoolean","COPY",EDGE,{"derivedFrom":makeQuery(id+"F3.opExtrude","CAP_EDGE",EDGE,{"disambiguationData":[OSD([sQuery(id+"F2.wireOp",EDGE,"E8")])],"isStart":true})});
            fillet(context, id + "F30", {"entities" : qUnion([Q0, Q1]), "radius" : 1 * mm, "tangentPropagation" : true, "allowEdgeOverflow" : false});
        }
    });
